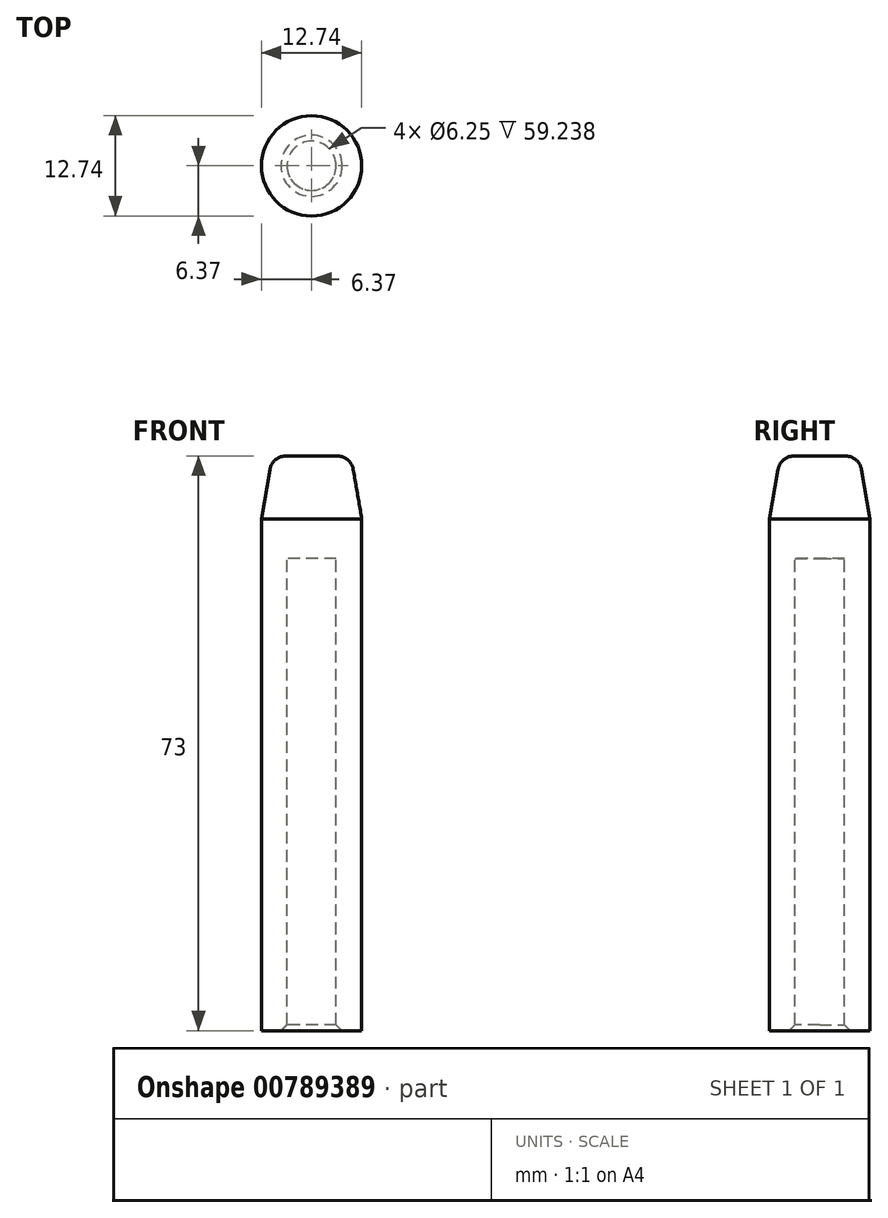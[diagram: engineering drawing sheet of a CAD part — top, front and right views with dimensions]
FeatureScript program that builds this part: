
annotation { "Feature Type Name" : "Feature", "Feature Type Description" : "" }
export const myFeature = defineFeature(function(context is Context, id is Id, definition is map)
    precondition{}
    {
        {
            var Q0;
            Q0=qCreatedBy(makeId("Front.planeOp"),FACE);
            var sketch = newSketch(context, id + "F0", { "sketchPlane" : qUnion([Q0])});
            skLineSegment(sketch, "E0", {"start": v(-6.37, 0) * mm, "end": v(-3.13, 0) * mm});
            skLineSegment(sketch, "E1", {"start": v(-6.37, 0) * mm, "end": v(-6.37, 65) * mm});
            skLineSegment(sketch, "E2", {"start": v(-6.37, 65) * mm, "end": v(-5, 73) * mm});
            skLineSegment(sketch, "E3", {"start": v(-5, 73) * mm, "end": v(0, 73) * mm});
            skLineSegment(sketch, "E4", {"start": v(0, 73) * mm, "end": v(0, 60) * mm});
            skLineSegment(sketch, "E5", {"start": v(0, 60) * mm, "end": v(-3.13, 60) * mm});
            skLineSegment(sketch, "E6", {"start": v(-3.13, 60) * mm, "end": v(-3.13, 0) * mm});
            skPoint(sketch, "E7.orphan", {"position": v(0, 0) * mm});
            skSolve(sketch);
        }
        {
            var Q0;
            Q0=makeQuery(id+"F0.imprint","IMPRINT",FACE,{"disambiguationData":[TD([[makeQuery(id+"F0.imprint","IMPRINT",EDGE,{"derivedFrom":sQuery(id+"F0.wireOp",EDGE,"E0")}),1.0]])]});
            var Q1;
            Q1=sQuery(id+"F0.wireOp",EDGE,"E4");
            revolve(context, id + "F1", {"surfaceOperationType" : NewSurfaceOperationType.NEW, "entities" : qUnion([Q0]), "axis" : qUnion([Q1]), "revolveType" : RevolveType.FULL});
        }
        {
            var Q0;
            Q0=makeQuery(id+"F1.opRevolve","SWEPT_EDGE",EDGE,{"disambiguationData":[OSD([sQuery(id+"F0.wireOp",EDGE,"E2"),sQuery(id+"F0.wireOp",EDGE,"E3")])]});
            fillet(context, id + "F2", {"entities" : qUnion([Q0]), "radius" : 2.03 * mm, "tangentPropagation" : true, "allowEdgeOverflow" : false});
        }
        {
            var Q0;
            Q0=makeQuery(id+"F1.opRevolve","SWEPT_EDGE",EDGE,{"disambiguationData":[OSD([sQuery(id+"F0.wireOp",EDGE,"E0"),sQuery(id+"F0.wireOp",EDGE,"E6")])]});
            chamfer(context, id + "F3", {"entities" : qUnion([Q0]), "width" : 0.76 * mm, "tangentPropagation" : true});
        }
    });
